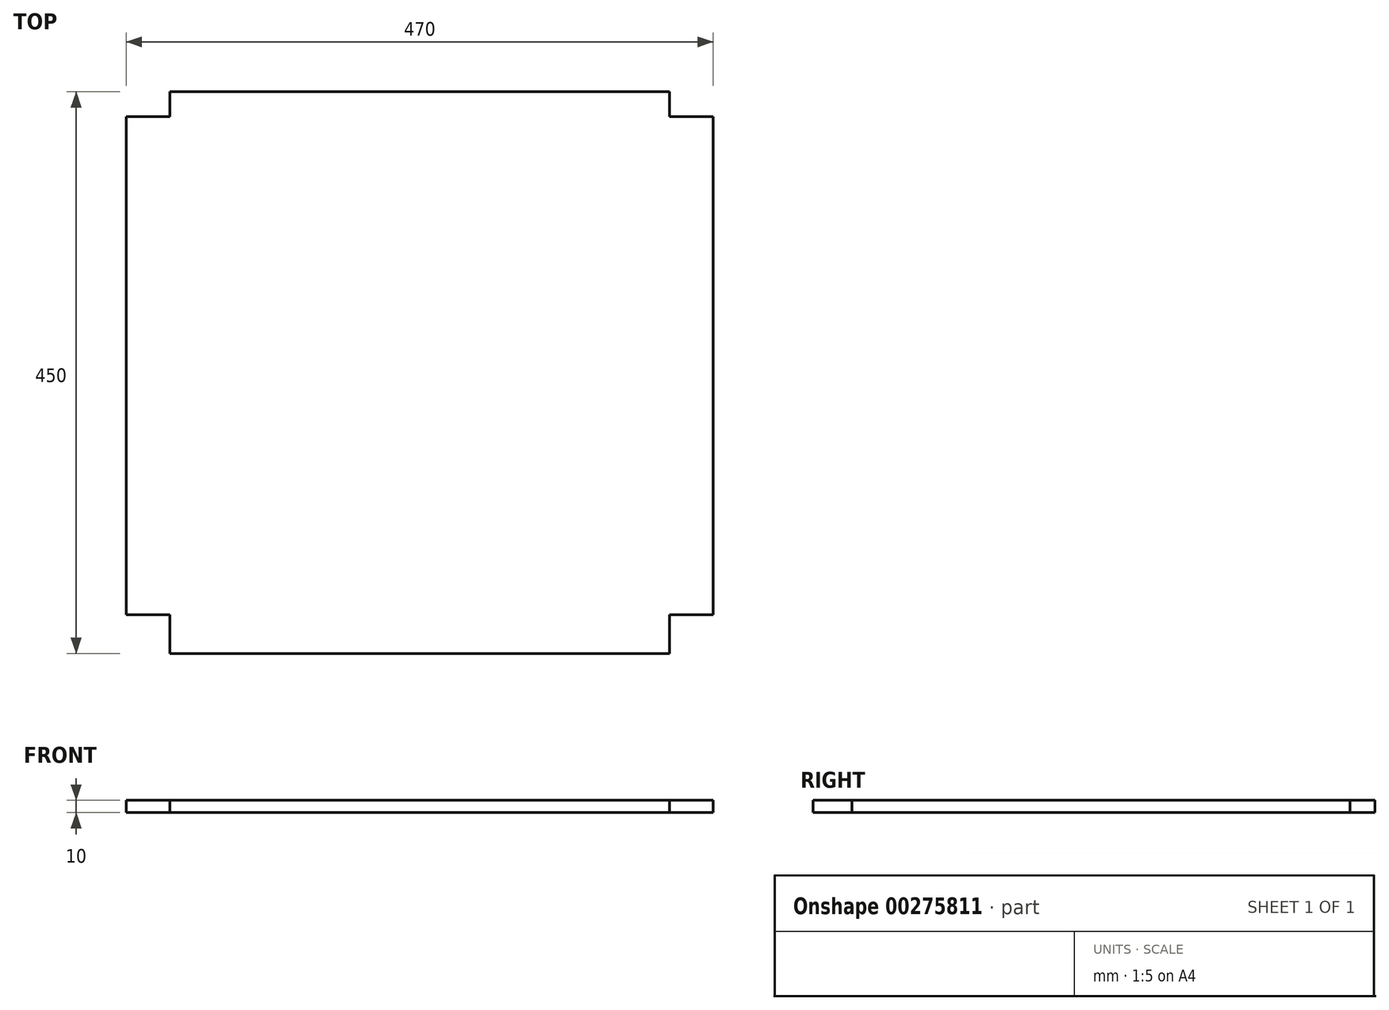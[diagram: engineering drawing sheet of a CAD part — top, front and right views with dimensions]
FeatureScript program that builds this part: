
annotation { "Feature Type Name" : "Feature", "Feature Type Description" : "" }
export const myFeature = defineFeature(function(context is Context, id is Id, definition is map)
    precondition{}
    {
        {
            var Q0;
            Q0=qCreatedBy(makeId("Top.planeOp"),FACE);
            var sketch = newSketch(context, id + "F0", { "sketchPlane" : qUnion([Q0])});
            skLineSegment(sketch, "E0", {"start": v(0, 0) * mm, "end": v(470, 0) * mm});
            skLineSegment(sketch, "E1", {"start": v(470, 0) * mm, "end": v(470, 450) * mm});
            skLineSegment(sketch, "E2", {"start": v(470, 450) * mm, "end": v(0, 450) * mm});
            skLineSegment(sketch, "E3", {"start": v(0, 450) * mm, "end": v(0, 0) * mm});
            skSolve(sketch);
        }
        {
            var Q0;
            Q0=qSketchRegion(id+"F0",true);
            extrude(context, id + "F1", {"entities" : qUnion([Q0]), "depth" : 10 * mm});
        }
        {
            var Q0;
            Q0=makeQuery(id+"F1.opExtrude","CAP_FACE",FACE,{"disambiguationData":[OSD([sQuery(id+"F0.wireOp",EDGE,"E0"),sQuery(id+"F0.wireOp",EDGE,"E1"),sQuery(id+"F0.wireOp",EDGE,"E2"),sQuery(id+"F0.wireOp",EDGE,"E3")])],"isStart":false});
            var sketch = newSketch(context, id + "F2", { "sketchPlane" : qUnion([Q0])});
            skLineSegment(sketch, "E4.bottom", {"start": v(35, 450) * mm, "end": v(0, 450) * mm});
            skLineSegment(sketch, "E4.top", {"start": v(35, 430) * mm, "end": v(0, 430) * mm});
            skLineSegment(sketch, "E4.left", {"start": v(35, 450) * mm, "end": v(35, 430) * mm});
            skLineSegment(sketch, "E4.right", {"start": v(0, 450) * mm, "end": v(0, 430) * mm});
            skLineSegment(sketch, "E5.bottom", {"start": v(0, 0) * mm, "end": v(35, 0) * mm});
            skLineSegment(sketch, "E5.top", {"start": v(0, 31) * mm, "end": v(35, 31) * mm});
            skLineSegment(sketch, "E5.left", {"start": v(0, 0) * mm, "end": v(0, 31) * mm});
            skLineSegment(sketch, "E5.right", {"start": v(35, 0) * mm, "end": v(35, 31) * mm});
            skLineSegment(sketch, "E6", {"start": v(235, 450) * mm, "end": v(235, 0) * mm, "construction": true});
            skLineSegment(sketch, "E7.MirrorCS", {"start": v(470, 450) * mm, "end": v(470, 430) * mm});
            skLineSegment(sketch, "E8.MirrorCS", {"start": v(435, 450) * mm, "end": v(470, 450) * mm});
            skLineSegment(sketch, "E9.MirrorCS", {"start": v(435, 430) * mm, "end": v(470, 430) * mm});
            skLineSegment(sketch, "E10.MirrorCS", {"start": v(435, 450) * mm, "end": v(435, 430) * mm});
            skLineSegment(sketch, "E11.MirrorCS", {"start": v(470, 31) * mm, "end": v(435, 31) * mm});
            skLineSegment(sketch, "E12.MirrorCS", {"start": v(470, 0) * mm, "end": v(435, 0) * mm});
            skLineSegment(sketch, "E13.MirrorCS", {"start": v(435, 0) * mm, "end": v(435, 31) * mm});
            skLineSegment(sketch, "E14.MirrorCS", {"start": v(470, 0) * mm, "end": v(470, 31) * mm});
            skSolve(sketch);
        }
        {
            var Q0;
            Q0=qSketchRegion(id+"F2",true);
            var Q1;
            Q1 = qSketchRegion(id + "F0", true);
            extrude(context, id + "F3", {"entities" : qUnion([Q0, Q1]), "operationType" : NewBodyOperationType.REMOVE, "endBound" : BoundingType.THROUGH_ALL, "oppositeDirection" : true, "depth" : 25 * mm});
        }
    });
